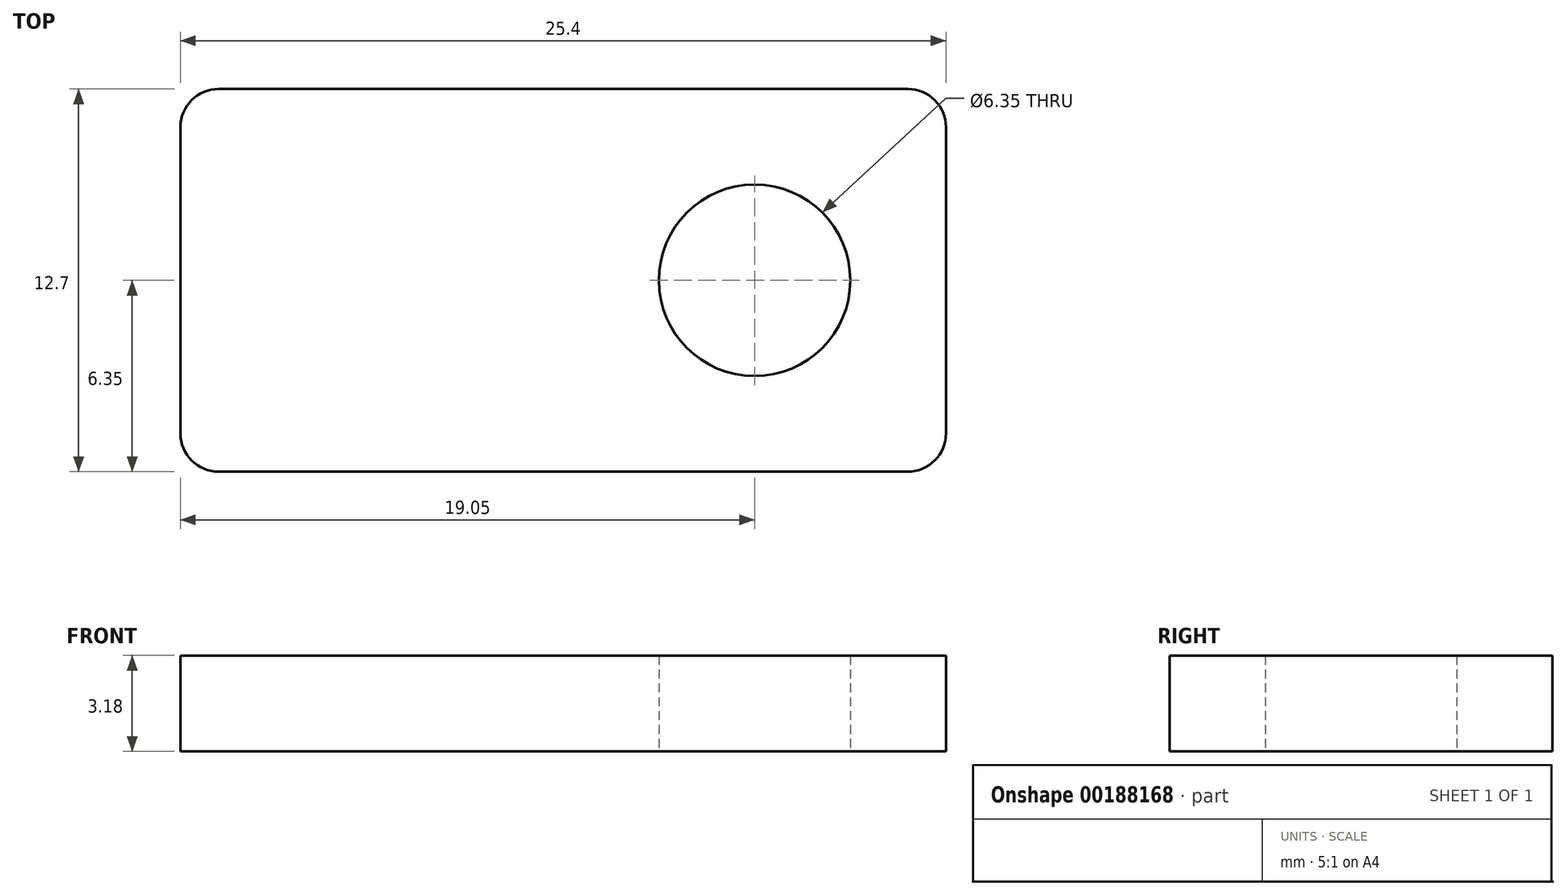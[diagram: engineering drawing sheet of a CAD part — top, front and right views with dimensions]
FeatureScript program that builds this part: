
annotation { "Feature Type Name" : "Feature", "Feature Type Description" : "" }
export const myFeature = defineFeature(function(context is Context, id is Id, definition is map)
    precondition{}
    {
        {
            var Q0;
            Q0=qCreatedBy(makeId("Top.planeOp"),FACE);
            var sketch = newSketch(context, id + "F0", { "sketchPlane" : qUnion([Q0])});
            skLineSegment(sketch, "E0.bottom", {"start": v(11.43, 6.35) * mm, "end": v(-11.43, 6.35) * mm});
            skLineSegment(sketch, "E0.top", {"start": v(11.43, -6.35) * mm, "end": v(-11.43, -6.35) * mm});
            skLineSegment(sketch, "E0.left", {"start": v(12.7, 5.08) * mm, "end": v(12.7, -5.08) * mm});
            skLineSegment(sketch, "E0.right", {"start": v(-12.7, 5.08) * mm, "end": v(-12.7, -5.08) * mm});
            skPoint(sketch, "E1.visualSharp", {"position": v(-12.7, 6.35) * mm});
            skArc(sketch, "E1.filletArc", {"start": v(-11.43, 6.35) * mm, "mid": v(-12.33, 5.98) * mm, "end": v(-12.7, 5.08) * mm});
            skPoint(sketch, "E2.visualSharp", {"position": v(12.7, 6.35) * mm});
            skArc(sketch, "E2.filletArc", {"start": v(12.7, 5.08) * mm, "mid": v(12.33, 5.98) * mm, "end": v(11.43, 6.35) * mm});
            skPoint(sketch, "E3.visualSharp", {"position": v(12.7, -6.35) * mm});
            skArc(sketch, "E3.filletArc", {"start": v(11.43, -6.35) * mm, "mid": v(12.33, -5.98) * mm, "end": v(12.7, -5.08) * mm});
            skPoint(sketch, "E4.visualSharp", {"position": v(-12.7, -6.35) * mm});
            skArc(sketch, "E4.filletArc", {"start": v(-12.7, -5.08) * mm, "mid": v(-12.33, -5.98) * mm, "end": v(-11.43, -6.35) * mm});
            skCircle(sketch, "E5", {"center": v(6.35, 0) * mm, "radius": 3.18 * mm});
            skLineSegment(sketch, "E6", {"start": v(0, 0) * mm, "end": v(12.7, 0) * mm, "construction": true});
            skLineSegment(sketch, "E7", {"start": v(-12.7, 0) * mm, "end": v(12.7, 0) * mm, "construction": true});
            skSolve(sketch);
        }
        {
            var Q0;
            Q0=makeQuery(id+"F0.imprint","IMPRINT",FACE,{"disambiguationData":[TD([[makeQuery(id+"F0.imprint","IMPRINT",EDGE,{"derivedFrom":sQuery(id+"F0.wireOp",EDGE,"E0.bottom")}),1.0]])]});
            extrude(context, id + "F1", {"entities" : qUnion([Q0]), "depth" : 3.17 * mm});
        }
    });
